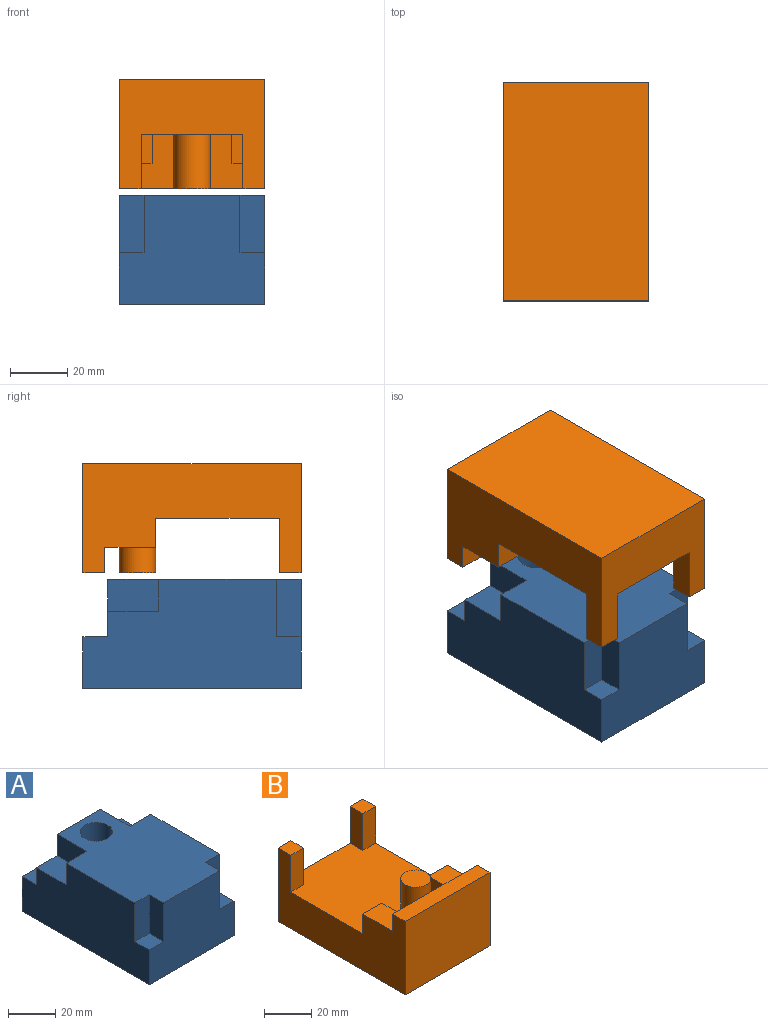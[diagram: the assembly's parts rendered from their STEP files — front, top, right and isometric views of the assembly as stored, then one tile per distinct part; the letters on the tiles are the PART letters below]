
ASSEMBLY  parts=2 mates=1
PART A: 22 faces, bbox 50.8x76.2x38.1 mm
  f0: plane 76.2x38.1mm, normal (1,0,0), area 2357.9mm2, adj f1,f2,f4,f5,f6,f7,f9,f10
  f1: plane 50.8x38.1mm, normal (0,-1,0), area 1588.9mm2, adj f0,f2,f3,f5,f16,f18,f19,f21
  f2: plane 67.56x50.8mm, normal (0,0,1), area 2692.8mm2, adj f0,f1,f3,f6,f8,f9,f11,f12
  f3: plane 76.2x38.1mm, normal (-1,0,0), area 2357.9mm2, adj f1,f2,f4,f5,f6,f7,f11,f13
  f4: plane 50.8x18.03mm, normal (0,1,0), area 916.1mm2, adj f0,f3,f5,f7
  f5: plane 76.2x50.8mm, normal (0,0,-1), area 3871mm2, adj f0,f1,f3,f4
  f6: plane 50.8x20.07mm, normal (0,1,0), area 741.2mm2, adj f0,f2,f3,f7,f8,f10,f12,f13
  f7: plane 50.8x8.64mm, normal (0,0,1), area 438.7mm2, adj f0,f3,f4,f6
  f8: plane 17.78x11.18mm, normal (1,0,0), area 198.7mm2, adj f2,f6,f9,f10
  f9: plane 12.45x11.18mm, normal (0,1,0), area 139.1mm2, adj f0,f2,f8,f10
  f10: plane 17.78x12.45mm, normal (0,0,1), area 221.3mm2, adj f0,f6,f8,f9
  f11: plane 12.45x11.18mm, normal (0,1,0), area 139.1mm2, adj f2,f3,f12,f13
  f12: plane 17.78x11.18mm, normal (-1,0,0), area 198.7mm2, adj f2,f6,f11,f13
  f13: plane 17.78x12.45mm, normal (0,0,1), area 221.3mm2, adj f3,f6,f11,f12
  f14: cylinder r=6.86mm len=20.07mm, axis (0,0,1), area 864.6mm2, adj f2,f15
  f15: plane 13.72x13.72mm, normal (0,0,1), area 147.8mm2, adj f14
  f16: plane 20.07x8.64mm, normal (-1,0,0), area 173.3mm2, adj f1,f2,f17,f18
  f17: plane 20.07x8.64mm, normal (0,-1,0), area 173.3mm2, adj f2,f3,f16,f18
  f18: plane 8.64x8.64mm, normal (0,0,1), area 74.6mm2, adj f1,f3,f16,f17
  f19: plane 20.07x8.64mm, normal (1,0,0), area 173.3mm2, adj f1,f2,f20,f21
  f20: plane 20.07x8.64mm, normal (0,-1,0), area 173.3mm2, adj f0,f2,f19,f21
  f21: plane 8.64x8.64mm, normal (0,0,1), area 74.6mm2, adj f0,f1,f19,f20
PART B: 22 faces, bbox 50.8x76.2x38.1 mm
  f0: plane 76.2x38.1mm, normal (-1,0,0), area 1922.6mm2, adj f1,f2,f4,f6,f7,f8,f14,f15
  f1: plane 50.8x7.62mm, normal (0,0,1), area 387.1mm2, adj f0,f4,f5,f8
  f2: plane 7.62x7.62mm, normal (0,0,1), area 58.1mm2, adj f0,f6,f13,f14
  f3: plane 7.62x7.62mm, normal (0,0,1), area 58.1mm2, adj f5,f6,f11,f12
  f4: plane 50.8x38.1mm, normal (0,-1,0), area 1935.5mm2, adj f0,f1,f5,f7
  f5: plane 76.2x38.1mm, normal (1,0,0), area 1922.6mm2, adj f1,f3,f4,f6,f7,f8,f10,f11
  f6: plane 50.8x38.1mm, normal (0,1,0), area 1258.1mm2, adj f0,f2,f3,f5,f7,f12,f13,f18
  f7: plane 76.2x50.8mm, normal (0,0,-1), area 3871mm2, adj f0,f4,f5,f6
  f8: plane 50.8x19.05mm, normal (0,1,0), area 735.5mm2, adj f0,f1,f5,f9,f17,f18,f20,f21
  f9: plane 17.78x10.16mm, normal (-1,0,0), area 180.6mm2, adj f8,f10,f18,f21
  f10: plane 11.43x10.16mm, normal (0,1,0), area 116.1mm2, adj f5,f9,f18,f21
  f11: plane 19.05x7.62mm, normal (0,-1,0), area 145.2mm2, adj f3,f5,f12,f18
  f12: plane 19.05x7.62mm, normal (-1,0,0), area 145.2mm2, adj f3,f6,f11,f18
  f13: plane 19.05x7.62mm, normal (1,0,0), area 145.2mm2, adj f2,f6,f14,f18
  f14: plane 19.05x7.62mm, normal (0,-1,0), area 145.2mm2, adj f0,f2,f13,f18
  f15: plane 11.43x10.16mm, normal (0,1,0), area 116.1mm2, adj f0,f17,f18,f20
  f16: cylinder r=6.35mm len=19.05mm, axis (0,0,1), area 760.1mm2, adj f18,f19
  f17: plane 17.78x10.16mm, normal (1,0,0), area 180.6mm2, adj f8,f15,f18,f20
  f18: plane 68.58x50.8mm, normal (0,0,1), area 2834.6mm2, adj f0,f5,f6,f8,f9,f10,f11,f12
  f19: plane 12.7x12.7mm, normal (0,0,1), area 126.7mm2, adj f16
  f20: plane 17.78x11.43mm, normal (0,0,1), area 203.2mm2, adj f0,f8,f15,f17
  f21: plane 17.78x11.43mm, normal (0,0,1), area 203.2mm2, adj f5,f8,f9,f10
PLACE A t=(-53.18,-4.94,-34.85)mm fixed
PLACE B rot(axis=(1,0,0),180deg) t=(-53.18,-4.94,24.67)mm
MATE slider B.f16 <-> A.f14  axis (0,0,-1) through (-53.18,14.11,5.62)mm
